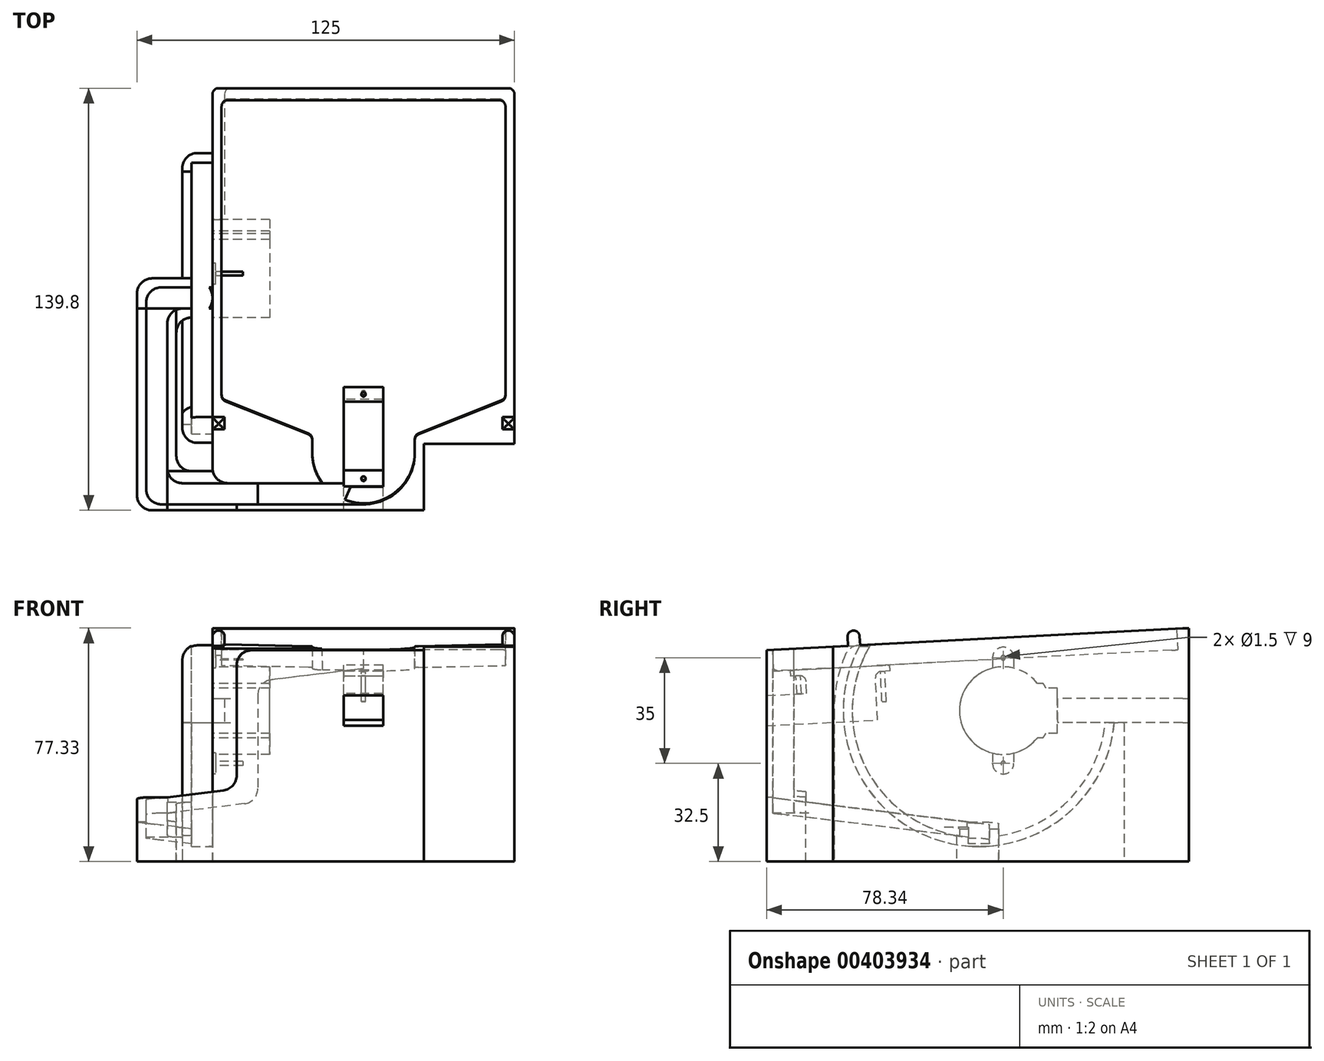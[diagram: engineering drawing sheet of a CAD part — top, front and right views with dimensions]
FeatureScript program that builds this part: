
annotation { "Feature Type Name" : "Feature", "Feature Type Description" : "" }
export const myFeature = defineFeature(function(context is Context, id is Id, definition is map)
    precondition{}
    {
        {
            var Q0;
            Q0=qCreatedBy(makeId("Right.planeOp"),FACE);
            var sketch = newSketch(context, id + "F0", { "sketchPlane" : qUnion([Q0])});
            skLineSegment(sketch, "E0", {"start": v(-65.34, 50) * mm, "end": v(-65.34, -20) * mm});
            skLineSegment(sketch, "E1", {"start": v(-65.34, -20) * mm, "end": v(74.46, -20) * mm});
            skLineSegment(sketch, "E2", {"start": v(74.46, -20) * mm, "end": v(74.46, 57.33) * mm});
            skLineSegment(sketch, "E3", {"start": v(74.46, 57.33) * mm, "end": v(-65.34, 50) * mm});
            skPoint(sketch, "E4", {"position": v(0, 53.42) * mm});
            skPoint(sketch, "E5", {"position": v(0, 46.41) * mm});
            skSolve(sketch);
        }
        {
            var Q0;
            Q0=qSketchRegion(id+"F0",true);
            extrude(context, id + "F1", {"entities" : qUnion([Q0]), "depth" : 50 * mm, "hasSecondDirection" : true, "secondDirectionOppositeDirection" : true, "secondDirectionDepth" : 50 * mm});
        }
        {
            var Q0;
            Q0=makeQuery(id+"F1.opExtrude","SWEPT_FACE",FACE,{"disambiguationData":[OSD([sQuery(id+"F0.wireOp",EDGE,"E3")])]});
            var sketch = newSketch(context, id + "F2", { "sketchPlane" : qUnion([Q0])});
            skPoint(sketch, "E6.endSnap0", {"position": v(0, -57.54) * mm});
            skPoint(sketch, "E6.end.orphan", {"position": v(0, -83) * mm});
            skPoint(sketch, "E7.orphan", {"position": v(-48, -57.54) * mm});
            skPoint(sketch, "E8.orphan", {"position": v(48, -57.54) * mm});
            skLineSegment(sketch, "E9.0", {"start": v(47, 73.36) * mm, "end": v(-47, 73.36) * mm});
            skLineSegment(sketch, "E9.1", {"start": v(47, 73.36) * mm, "end": v(47, -25.96) * mm});
            skLineSegment(sketch, "E9.2", {"start": v(-47, 73.36) * mm, "end": v(-47, -25.96) * mm});
            skLineSegment(sketch, "E9.3", {"start": v(17, -37.96) * mm, "end": v(47, -25.96) * mm});
            skLineSegment(sketch, "E9.4", {"start": v(-17, -37.96) * mm, "end": v(-47, -25.96) * mm});
            skLineSegment(sketch, "E9.5", {"start": v(-17, -43.64) * mm, "end": v(-17, -37.96) * mm});
            skArc(sketch, "E9.6", {"start": v(-17, -43.64) * mm, "mid": v(0, -60.64) * mm, "end": v(17, -43.64) * mm});
            skLineSegment(sketch, "E9.7", {"start": v(17, -43.64) * mm, "end": v(17, -37.96) * mm});
            skPoint(sketch, "E10.bottom.end.orphan", {"position": v(-48, 78.46) * mm});
            skPoint(sketch, "E10.bottom.start.orphan", {"position": v(48, 78.46) * mm});
            skPoint(sketch, "E11", {"position": v(0, 2.8) * mm});
            skSolve(sketch);
        }
        {
            var Q0;
            Q0=makeQuery(id+"F2.imprint","IMPRINT",FACE,{"disambiguationData":[TD([[makeQuery(id+"F2.imprint","IMPRINT",EDGE,{"derivedFrom":sQuery(id+"F2.wireOp",EDGE,"E9.0")}),1.0]])]});
            cPlane(context, id + "F3", {"entities" : qUnion([Q0]), "cplaneType" : CPlaneType.OFFSET, "offset" : 7 * mm, "oppositeDirection" : true, "width" : 150 * mm, "height" : 150 * mm});
        }
        {
            var Q0;
            Q0=qCreatedBy(id+"F3.planeOp",FACE);
            var sketch = newSketch(context, id + "F4", { "sketchPlane" : qUnion([Q0])});
            skPoint(sketch, "E12", {"position": v(0, 2.43) * mm});
            skPoint(sketch, "E13.endSnap0", {"position": v(0, -58.41) * mm});
            skPoint(sketch, "E13.end.orphan", {"position": v(0, -83.88) * mm});
            skPoint(sketch, "E14.orphan", {"position": v(-48, -58.41) * mm});
            skPoint(sketch, "E15.orphan", {"position": v(48, -58.41) * mm});
            skLineSegment(sketch, "E16.0", {"start": v(47, 73.36) * mm, "end": v(-47, 73.36) * mm});
            skLineSegment(sketch, "E16.1", {"start": v(47, 73.36) * mm, "end": v(47, -25.96) * mm});
            skLineSegment(sketch, "E16.2", {"start": v(-47, 73.36) * mm, "end": v(-47, -25.96) * mm});
            skLineSegment(sketch, "E16.3", {"start": v(17, -37.96) * mm, "end": v(47, -25.96) * mm});
            skLineSegment(sketch, "E16.4", {"start": v(-17, -37.96) * mm, "end": v(-47, -25.96) * mm});
            skLineSegment(sketch, "E16.5", {"start": v(-17, -43.64) * mm, "end": v(-17, -37.96) * mm});
            skArc(sketch, "E16.6", {"start": v(-17, -43.64) * mm, "mid": v(0, -60.64) * mm, "end": v(17, -43.64) * mm});
            skLineSegment(sketch, "E16.7", {"start": v(17, -43.64) * mm, "end": v(17, -37.96) * mm});
            skPoint(sketch, "E17.bottom.end.orphan", {"position": v(-48, 77.59) * mm});
            skPoint(sketch, "E17.bottom.start.orphan", {"position": v(48, 77.59) * mm});
            skSolve(sketch);
        }
        {
            var Q1;
            Q1=qSketchRegion(id+"F2",true);
            var Q2;
            Q2=qSketchRegion(id+"F4",true);
            loft(context, id + "F5", {"operationType" : NewBodyOperationType.REMOVE, "sheetProfilesArray" : [{ "sheetProfileEntities" : qUnion([Q1]) }, { "sheetProfileEntities" : qUnion([Q2]) }]});
        }
        {
            var Q0;
            Q0=makeQuery(id+"F1.opExtrude","CAP_FACE",FACE,{"disambiguationData":[OSD([sQuery(id+"F0.wireOp",EDGE,"E0"),sQuery(id+"F0.wireOp",EDGE,"E1"),sQuery(id+"F0.wireOp",EDGE,"E2"),sQuery(id+"F0.wireOp",EDGE,"E3")])],"isStart":true});
            var sketch = newSketch(context, id + "F6", { "sketchPlane" : qUnion([Q0])});
            skArc(sketch, "E18", {"start": v(-24.37, 21) * mm, "mid": v(1.5, 30) * mm, "end": v(-24.37, 39) * mm});
            skPoint(sketch, "E19", {"position": v(-5, 30) * mm});
            skLineSegment(sketch, "E20.bottom", {"start": v(-31, 22.5) * mm, "end": v(-27.13, 22.5) * mm});
            skLineSegment(sketch, "E20.top", {"start": v(-31, 37.5) * mm, "end": v(-27.13, 37.5) * mm});
            skLineSegment(sketch, "E20.left", {"start": v(-31, 22.5) * mm, "end": v(-31, 37.5) * mm});
            skArc(sketch, "E21", {"start": v(-26.23, 39) * mm, "mid": v(-26.7, 38.26) * mm, "end": v(-27.13, 37.5) * mm});
            skLineSegment(sketch, "E22.bottom", {"start": v(-26.23, 39) * mm, "end": v(-24.37, 39) * mm});
            skLineSegment(sketch, "E22.top", {"start": v(-26.23, 21) * mm, "end": v(-24.37, 21) * mm});
            skArc(sketch, "E23.trimOffspring", {"start": v(-27.13, 22.5) * mm, "mid": v(-26.7, 21.74) * mm, "end": v(-26.23, 21) * mm});
            skSolve(sketch);
        }
        {
            var Q0;
            Q0=qSketchRegion(id+"F6",true);
            extrude(context, id + "F7", {"entities" : qUnion([Q0]), "operationType" : NewBodyOperationType.REMOVE, "oppositeDirection" : true, "depth" : 19 * mm});
        }
        {
            var Q0;
            Q0=makeQuery(id+"F1.opExtrude","CAP_FACE",FACE,{"disambiguationData":[OSD([sQuery(id+"F0.wireOp",EDGE,"E0"),sQuery(id+"F0.wireOp",EDGE,"E1"),sQuery(id+"F0.wireOp",EDGE,"E2"),sQuery(id+"F0.wireOp",EDGE,"E3")])],"isStart":true});
            var sketch = newSketch(context, id + "F8", { "sketchPlane" : qUnion([Q0])});
            skLineSegment(sketch, "E24", {"start": v(-13, 47.5) * mm, "end": v(-13, 12.5) * mm});
            skPoint(sketch, "E25", {"position": v(-13, 30) * mm});
            skArc(sketch, "E26.0.startCap", {"start": v(-16.5, 47.5) * mm, "mid": v(-13, 51) * mm, "end": v(-9.5, 47.5) * mm});
            skArc(sketch, "E26.0.endCap", {"start": v(-9.5, 12.5) * mm, "mid": v(-13, 9) * mm, "end": v(-16.5, 12.5) * mm});
            skLineSegment(sketch, "E26.0.left", {"start": v(-9.5, 47.5) * mm, "end": v(-9.5, 12.5) * mm});
            skLineSegment(sketch, "E26.0.right", {"start": v(-16.5, 47.5) * mm, "end": v(-16.5, 12.5) * mm});
            skSolve(sketch);
        }
        {
            var Q0;
            Q0=qSketchRegion(id+"F8",true);
            extrude(context, id + "F9", {"entities" : qUnion([Q0]), "operationType" : NewBodyOperationType.REMOVE, "oppositeDirection" : true, "depth" : 1 * mm});
        }
        {
            var Q0;
            Q0=makeQuery(id+"F1.opExtrude","CAP_FACE",FACE,{"disambiguationData":[OSD([sQuery(id+"F0.wireOp",EDGE,"E0"),sQuery(id+"F0.wireOp",EDGE,"E1"),sQuery(id+"F0.wireOp",EDGE,"E2"),sQuery(id+"F0.wireOp",EDGE,"E3")])],"isStart":true});
            var sketch = newSketch(context, id + "F10", { "sketchPlane" : qUnion([Q0])});
            skLineSegment(sketch, "E27.bottom", {"start": v(-81, 34) * mm, "end": v(-21, 34) * mm});
            skLineSegment(sketch, "E27.top", {"start": v(-81, 26) * mm, "end": v(-21, 26) * mm});
            skLineSegment(sketch, "E27.left", {"start": v(-81, 34) * mm, "end": v(-81, 26) * mm});
            skLineSegment(sketch, "E27.right", {"start": v(-21, 34) * mm, "end": v(-21, 26) * mm});
            skPoint(sketch, "E27.middle", {"position": v(-51, 30) * mm});
            skSolve(sketch);
        }
        {
            var Q0;
            Q0=qSketchRegion(id+"F10",true);
            extrude(context, id + "F11", {"entities" : qUnion([Q0]), "operationType" : NewBodyOperationType.REMOVE, "oppositeDirection" : true, "depth" : 4 * mm});
        }
        {
            var Q0;
            Q0=qCreatedBy(makeId("Front.planeOp"),FACE);
            cPlane(context, id + "F12", {"entities" : qUnion([Q0]), "cplaneType" : CPlaneType.OFFSET, "offset" : 5 * mm, "oppositeDirection" : true, "width" : 150 * mm, "height" : 150 * mm});
        }
        {
            var Q0;
            Q0=qCreatedBy(id+"F12.planeOp",FACE);
            var sketch = newSketch(context, id + "F13", { "sketchPlane" : qUnion([Q0])});
            skLineSegment(sketch, "E28", {"start": v(-50, -20) * mm, "end": v(-75, -20) * mm});
            skLineSegment(sketch, "E29", {"start": v(-50, -9.96) * mm, "end": v(-75, -6.9) * mm});
            skLineSegment(sketch, "E30", {"start": v(-75, -20) * mm, "end": v(-75, -6.9) * mm});
            skLineSegment(sketch, "E31", {"start": v(-50, -20) * mm, "end": v(-50, -9.96) * mm});
            skSolve(sketch);
        }
        {
            var Q0;
            Q0=qSketchRegion(id+"F13",true);
            extrude(context, id + "F14", {"entities" : qUnion([Q0]), "operationType" : NewBodyOperationType.ADD, "depth" : 6.5 * mm, "hasSecondDirection" : true, "secondDirectionOppositeDirection" : true, "secondDirectionDepth" : 6.5 * mm});
        }
        {
            var Q0;
            Q0=makeQuery(id+"F2.imprint","IMPRINT",FACE,{"disambiguationData":[TD([[makeQuery(id+"F2.imprint","IMPRINT",EDGE,{"derivedFrom":sQuery(id+"F2.wireOp",EDGE,"E9.0")}),1.0]])]});
            var sketch = newSketch(context, id + "F15", { "sketchPlane" : qUnion([Q0])});
            skLineSegment(sketch, "E32.bottom", {"start": v(6.5, -50.14) * mm, "end": v(-6.5, -50.14) * mm});
            skLineSegment(sketch, "E32.top", {"start": v(6.5, -27.14) * mm, "end": v(-6.5, -27.14) * mm});
            skLineSegment(sketch, "E32.left", {"start": v(6.5, -50.14) * mm, "end": v(6.5, -27.14) * mm});
            skLineSegment(sketch, "E32.right", {"start": v(-6.5, -50.14) * mm, "end": v(-6.5, -27.14) * mm});
            skPoint(sketch, "E32.middle", {"position": v(0, -38.64) * mm});
            skSolve(sketch);
        }
        {
            var Q0;
            Q0=qSketchRegion(id+"F15",true);
            extrude(context, id + "F16", {"entities" : qUnion([Q0]), "operationType" : NewBodyOperationType.REMOVE, "oppositeDirection" : true, "depth" : 25 * mm});
        }
        {
            var Q0;
            Q0=makeQuery(id+"F2.imprint","IMPRINT",FACE,{"disambiguationData":[TD([[makeQuery(id+"F2.imprint","IMPRINT",EDGE,{"derivedFrom":sQuery(id+"F2.wireOp",EDGE,"E9.0")}),1.0]])]});
            var sketch = newSketch(context, id + "F17", { "sketchPlane" : qUnion([Q0])});
            skLineSegment(sketch, "E33.bottom", {"start": v(6.5, -22.14) * mm, "end": v(-6.5, -22.14) * mm});
            skLineSegment(sketch, "E33.top", {"start": v(6.5, -55.14) * mm, "end": v(-6.5, -55.14) * mm});
            skLineSegment(sketch, "E33.left", {"start": v(6.5, -22.14) * mm, "end": v(6.5, -55.14) * mm});
            skLineSegment(sketch, "E33.right", {"start": v(-6.5, -22.14) * mm, "end": v(-6.5, -55.14) * mm});
            skPoint(sketch, "E33.middle", {"position": v(0, -38.64) * mm});
            skSolve(sketch);
        }
        {
            var Q0;
            Q0=qSketchRegion(id+"F17",true);
            extrude(context, id + "F18", {"entities" : qUnion([Q0]), "operationType" : NewBodyOperationType.REMOVE, "oppositeDirection" : true, "depth" : 9 * mm});
        }
        {
            var Q0;
            Q0=makeQuery(id+"FUqeBeKpT4LYNuk_1.boolean.opBoolean","MERGE",FACE,{"derivedFrom":[makeQuery(id+"F1.opExtrude","SWEPT_FACE",FACE,{"disambiguationData":[OSD([sQuery(id+"F0.wireOp",EDGE,"E0")])]}),makeQuery(id+"F61UTTqEWsXgY2D_1.opExtrude","SWEPT_FACE",FACE,{"disambiguationData":[OSD([sQuery(id+"F9Du9WT9e9JY5Dl_1.wireOp",EDGE,"sJgd1tPc-9qsz-vVnT-TqeQ-4TYIqpoZbmCu")])]}),makeQuery(id+"FUqeBeKpT4LYNuk_1.opExtrude","CAP_FACE",FACE,{"disambiguationData":[OSD([sQuery(id+"Fu5qXJoa0auTo1w_1.wireOp",EDGE,"depduNjt-3aMR-BOii-vv3o-0Txvqa5xbjUM"),sQuery(id+"Fu5qXJoa0auTo1w_1.wireOp",EDGE,"YClS0oY7-eXia-WmQ4-NOUT-qmrgQAcRW2ul"),sQuery(id+"Fu5qXJoa0auTo1w_1.wireOp",EDGE,"FjPESpCu-MEkZ-X1k0-rLkk-jPPFp3MV8du9"),sQuery(id+"Fu5qXJoa0auTo1w_1.wireOp",EDGE,"T3NzeVoH-fv4R-7HJz-S144-zwuEIWOQCuFN")])],"isStart":true})]});
            var sketch = newSketch(context, id + "F19", { "sketchPlane" : qUnion([Q0])});
            skLineSegment(sketch, "E34.bottom", {"start": v(50, -20) * mm, "end": v(20, -20) * mm});
            skLineSegment(sketch, "E34.top", {"start": v(50, 60) * mm, "end": v(20, 60) * mm});
            skLineSegment(sketch, "E34.left", {"start": v(50, -20) * mm, "end": v(50, 60) * mm});
            skLineSegment(sketch, "E34.right", {"start": v(20, -20) * mm, "end": v(20, 60) * mm});
            skSolve(sketch);
        }
        {
            var Q0;
            Q0=qSketchRegion(id+"F19",true);
            extrude(context, id + "F20", {"entities" : qUnion([Q0]), "operationType" : NewBodyOperationType.REMOVE, "oppositeDirection" : true, "depth" : 22 * mm});
        }
        {
            var Q0;
            Q0=makeQuery(id+"F16.boolean.opBoolean","COPY",FACE,{"derivedFrom":makeQuery(id+"F16.opExtrude","SWEPT_FACE",FACE,{"disambiguationData":[OSD([sQuery(id+"F15.wireOp",EDGE,"E32.bottom")])]})});
            var sketch = newSketch(context, id + "F21", { "sketchPlane" : qUnion([Q0])});
            skLineSegment(sketch, "E35.bottom", {"start": v(-6.5, 28.35) * mm, "end": v(6.5, 28.35) * mm});
            skLineSegment(sketch, "E35.top", {"start": v(-6.5, 38.35) * mm, "end": v(6.5, 38.35) * mm});
            skLineSegment(sketch, "E35.left", {"start": v(-6.5, 28.35) * mm, "end": v(-6.5, 38.35) * mm});
            skLineSegment(sketch, "E35.right", {"start": v(6.5, 28.35) * mm, "end": v(6.5, 38.35) * mm});
            skSolve(sketch);
        }
        {
            var Q0;
            Q0=qSketchRegion(id+"F21",true);
            extrude(context, id + "F22", {"entities" : qUnion([Q0]), "operationType" : NewBodyOperationType.REMOVE, "oppositeDirection" : true, "depth" : 25 * mm});
        }
        {
            var Q0;
            Q0=qCreatedBy(id+"F12.planeOp",FACE);
            var sketch = newSketch(context, id + "F23", { "sketchPlane" : qUnion([Q0])});
            skLineSegment(sketch, "E36", {"start": v(-50, -6.3) * mm, "end": v(-50, -15) * mm});
            skLineSegment(sketch, "E37", {"start": v(-50, -15) * mm, "end": v(-72, -12.3) * mm});
            skLineSegment(sketch, "E38", {"start": v(-72, -12.3) * mm, "end": v(-72, -6.3) * mm});
            skLineSegment(sketch, "E39", {"start": v(-72, -6.3) * mm, "end": v(-50, -6.3) * mm});
            skSolve(sketch);
        }
        {
            var Q0;
            Q0=qSketchRegion(id+"F23",true);
            extrude(context, id + "F24", {"entities" : qUnion([Q0]), "operationType" : NewBodyOperationType.REMOVE, "oppositeDirection" : true, "depth" : 3.5 * mm, "hasSecondDirection" : true, "secondDirectionOppositeDirection" : false, "secondDirectionDepth" : 3.5 * mm});
        }
        {
            var Q0;
            Q0=makeQuery(id+"F14.opExtrude","SWEPT_FACE",FACE,{"disambiguationData":[OSD([sQuery(id+"F13.wireOp",EDGE,"E30")])]});
            var sketch = newSketch(context, id + "F25", { "sketchPlane" : qUnion([Q0])});
            skLineSegment(sketch, "E40", {"start": v(1.5, -20) * mm, "end": v(65.34, -20) * mm});
            skLineSegment(sketch, "E41", {"start": v(65.34, -20) * mm, "end": v(65.34, 1.31) * mm});
            skLineSegment(sketch, "E42", {"start": v(65.34, 1.31) * mm, "end": v(-1.5, -6.9) * mm});
            skLineSegment(sketch, "E43", {"start": v(-1.5, -6.9) * mm, "end": v(-1.5, -20) * mm});
            skLineSegment(sketch, "E44", {"start": v(-1.5, -20) * mm, "end": v(1.5, -20) * mm});
            skSolve(sketch);
        }
        {
            var Q0;
            Q0=qSketchRegion(id+"F25",true);
            extrude(context, id + "F26", {"entities" : qUnion([Q0]), "operationType" : NewBodyOperationType.ADD, "oppositeDirection" : true, "depth" : 13 * mm});
        }
        {
            var Q0;
            Q0=makeQuery(id+"F26.boolean.opBoolean","MERGE",FACE,{"derivedFrom":[makeQuery(id+"F14.opExtrude","SWEPT_FACE",FACE,{"disambiguationData":[OSD([sQuery(id+"F13.wireOp",EDGE,"E30")])]}),makeQuery(id+"F26.opExtrude","CAP_FACE",FACE,{"disambiguationData":[OSD([sQuery(id+"F25.wireOp",EDGE,"E40"),sQuery(id+"F25.wireOp",EDGE,"E41"),sQuery(id+"F25.wireOp",EDGE,"E42"),sQuery(id+"F25.wireOp",EDGE,"E43"),sQuery(id+"F25.wireOp",EDGE,"E44")])],"isStart":true})]});
            cPlane(context, id + "F27", {"entities" : qUnion([Q0]), "cplaneType" : CPlaneType.OFFSET, "offset" : 3 * mm, "oppositeDirection" : true, "width" : 150 * mm, "height" : 150 * mm});
        }
        {
            var Q0;
            Q0=qCreatedBy(id+"F27.planeOp",FACE);
            var sketch = newSketch(context, id + "F28", { "sketchPlane" : qUnion([Q0])});
            skLineSegment(sketch, "E45", {"start": v(-1.5, -2.4) * mm, "end": v(-1.5, -11.93) * mm});
            skLineSegment(sketch, "E46", {"start": v(-1.5, -11.93) * mm, "end": v(63.34, -3.97) * mm});
            skLineSegment(sketch, "E47", {"start": v(63.34, -3.97) * mm, "end": v(63.34, 3.33) * mm});
            skLineSegment(sketch, "E48", {"start": v(63.34, 3.33) * mm, "end": v(-1.5, 3.33) * mm});
            skLineSegment(sketch, "E49", {"start": v(-1.5, 3.33) * mm, "end": v(-1.5, -2.4) * mm});
            skSolve(sketch);
        }
        {
            var Q0;
            Q0=qSketchRegion(id+"F28",true);
            extrude(context, id + "F29", {"entities" : qUnion([Q0]), "operationType" : NewBodyOperationType.REMOVE, "oppositeDirection" : true, "depth" : 7 * mm});
        }
        {
            var Q0;
            Q0=makeQuery(id+"F1.opExtrude","SWEPT_FACE",FACE,{"disambiguationData":[OSD([sQuery(id+"F0.wireOp",EDGE,"E0")])]});
            var sketch = newSketch(context, id + "F30", { "sketchPlane" : qUnion([Q0])});
            skLineSegment(sketch, "E50", {"start": v(-50, -20) * mm, "end": v(-50, 3.16) * mm});
            skLineSegment(sketch, "E51", {"start": v(-50, 3.16) * mm, "end": v(-65, 1.31) * mm});
            skLineSegment(sketch, "E52", {"start": v(-65, 1.31) * mm, "end": v(-65, -20) * mm});
            skLineSegment(sketch, "E53", {"start": v(-65, -20) * mm, "end": v(-50, -20) * mm});
            skSolve(sketch);
        }
        {
            var Q0;
            Q0=qSketchRegion(id+"F30",true);
            extrude(context, id + "F31", {"entities" : qUnion([Q0]), "operationType" : NewBodyOperationType.ADD, "oppositeDirection" : true, "depth" : 13 * mm});
        }
        {
            var Q0;
            Q0=makeQuery(id+"F29.boolean.opBoolean","COPY",FACE,{"derivedFrom":makeQuery(id+"F29.opExtrude","SWEPT_FACE",FACE,{"disambiguationData":[OSD([sQuery(id+"F28.wireOp",EDGE,"E47")])]})});
            var sketch = newSketch(context, id + "F32", { "sketchPlane" : qUnion([Q0])});
            skLineSegment(sketch, "E54", {"start": v(65, -3.97) * mm, "end": v(65, 76.03) * mm});
            skLineSegment(sketch, "E55", {"start": v(65, 76.03) * mm, "end": v(0, 76.03) * mm});
            skLineSegment(sketch, "E56", {"start": v(0, 76.03) * mm, "end": v(0, 43.93) * mm});
            skLineSegment(sketch, "E57", {"start": v(0, 43.93) * mm, "end": v(35, 39.63) * mm});
            skLineSegment(sketch, "E58", {"start": v(35, 39.63) * mm, "end": v(35, -0.29) * mm});
            skLineSegment(sketch, "E59", {"start": v(35, -0.29) * mm, "end": v(65, -3.97) * mm});
            skSolve(sketch);
        }
        {
            var Q0;
            Q0=qSketchRegion(id+"F32",true);
            extrude(context, id + "F33", {"entities" : qUnion([Q0]), "operationType" : NewBodyOperationType.REMOVE, "depth" : 7 * mm});
        }
        {
            var Q0;
            Q0=makeQuery(id+"F33.boolean.opBoolean","MERGE",FACE,{"derivedFrom":[makeQuery(id+"F29.boolean.opBoolean","COPY",FACE,{"derivedFrom":makeQuery(id+"F29.opExtrude","SWEPT_FACE",FACE,{"disambiguationData":[OSD([sQuery(id+"F28.wireOp",EDGE,"E47")])]})}),makeQuery(id+"F33.opExtrude","CAP_FACE",FACE,{"disambiguationData":[OSD([sQuery(id+"F32.wireOp",EDGE,"E54"),sQuery(id+"F32.wireOp",EDGE,"E55"),sQuery(id+"F32.wireOp",EDGE,"E56"),sQuery(id+"F32.wireOp",EDGE,"E57"),sQuery(id+"F32.wireOp",EDGE,"E58"),sQuery(id+"F32.wireOp",EDGE,"E59")])],"isStart":true})]});
            var sketch = newSketch(context, id + "F34", { "sketchPlane" : qUnion([Q0])});
            skLineSegment(sketch, "E60", {"start": v(50, 3.16) * mm, "end": v(42, 4.14) * mm});
            skLineSegment(sketch, "E61", {"start": v(42, 4.14) * mm, "end": v(42, 50.1) * mm});
            skLineSegment(sketch, "E62", {"start": v(42, 50.1) * mm, "end": v(50, 50.1) * mm});
            skLineSegment(sketch, "E63", {"start": v(50, 50.1) * mm, "end": v(50, 3.16) * mm});
            skSolve(sketch);
        }
        {
            var Q0;
            Q0=qSketchRegion(id+"F34",true);
            extrude(context, id + "F35", {"entities" : qUnion([Q0]), "operationType" : NewBodyOperationType.REMOVE, "oppositeDirection" : true, "depth" : 3 * mm});
        }
        {
            var Q0;
            Q0=makeQuery(id+"F6.imprint","IMPRINT",FACE,{"disambiguationData":[TD([[makeQuery(id+"F6.imprint","IMPRINT",EDGE,{"derivedFrom":sQuery(id+"F6.wireOp",EDGE,"E18")}),-1.0]])]});
            var sketch = newSketch(context, id + "F36", { "sketchPlane" : qUnion([Q0])});
            skArc(sketch, "E64", {"start": v(-49.82, 26) * mm, "mid": v(-37.7, -0.92) * mm, "end": v(-11.5, -14.53) * mm});
            skArc(sketch, "E65", {"start": v(43, 30) * mm, "mid": v(41.72, 41.01) * mm, "end": v(37.95, 51.44) * mm});
            skLineSegment(sketch, "E66", {"start": v(37.95, 51.44) * mm, "end": v(34.47, 51.62) * mm});
            skPoint(sketch, "E67", {"position": v(43, 30) * mm});
            skLineSegment(sketch, "E68", {"start": v(43, 30) * mm, "end": v(43, -20) * mm});
            skLineSegment(sketch, "E69", {"start": v(-53, 26) * mm, "end": v(-53, -20) * mm});
            skLineSegment(sketch, "E70", {"start": v(-53, -20) * mm, "end": v(43, -20) * mm});
            skLineSegment(sketch, "E71", {"start": v(-53, 26) * mm, "end": v(-49.82, 26) * mm});
            skLineSegment(sketch, "E72", {"start": v(-11.5, -14.53) * mm, "end": v(-11.5, -20) * mm});
            skLineSegment(sketch, "E73", {"start": v(1.5, -14.53) * mm, "end": v(1.5, -20) * mm});
            skArc(sketch, "E74.trimOffspring", {"start": v(1.5, -14.53) * mm, "mid": v(35.28, 9.93) * mm, "end": v(34.47, 51.62) * mm});
            skSolve(sketch);
        }
        {
            var Q0;
            Q0=qSketchRegion(id+"F36",true);
            extrude(context, id + "F37", {"entities" : qUnion([Q0]), "operationType" : NewBodyOperationType.ADD, "depth" : 10 * mm});
        }
        {
            var Q0;
            Q0=makeQuery(id+"F37.opExtrude","CAP_FACE",FACE,{"disambiguationData":[OSD([sQuery(id+"F36.wireOp",EDGE,"E64"),sQuery(id+"F36.wireOp",EDGE,"E69"),sQuery(id+"F36.wireOp",EDGE,"E70"),sQuery(id+"F36.wireOp",EDGE,"E71"),sQuery(id+"F36.wireOp",EDGE,"E72")])],"isStart":false});
            var sketch = newSketch(context, id + "F38", { "sketchPlane" : qUnion([Q0])});
            skArc(sketch, "E75", {"start": v(1.5, -14.53) * mm, "mid": v(35.28, 9.93) * mm, "end": v(34.47, 51.62) * mm});
            skArc(sketch, "E76", {"start": v(1.5, -11.5) * mm, "mid": v(33.1, 12.3) * mm, "end": v(30.9, 51.8) * mm});
            skLineSegment(sketch, "E77", {"start": v(-49.82, 26) * mm, "end": v(-46.8, 26) * mm});
            skLineSegment(sketch, "E78", {"start": v(34.47, 51.62) * mm, "end": v(30.9, 51.8) * mm});
            skLineSegment(sketch, "E79", {"start": v(-11.5, -14.53) * mm, "end": v(-11.5, -11.5) * mm});
            skLineSegment(sketch, "E80", {"start": v(1.5, -14.53) * mm, "end": v(1.5, -11.5) * mm});
            skArc(sketch, "E81.trimOffspring", {"start": v(-46.8, 26) * mm, "mid": v(-35.58, 1.2) * mm, "end": v(-11.5, -11.5) * mm});
            skArc(sketch, "E82.trimOffspring", {"start": v(-49.82, 26) * mm, "mid": v(-37.7, -0.92) * mm, "end": v(-11.5, -14.53) * mm});
            skSolve(sketch);
        }
        {
            var Q0;
            Q0=qSketchRegion(id+"F38",true);
            extrude(context, id + "F39", {"entities" : qUnion([Q0]), "operationType" : NewBodyOperationType.ADD, "oppositeDirection" : true, "depth" : 3 * mm});
        }
        {
            var Q0;
            Q0=makeQuery(id+"F6.imprint","IMPRINT",FACE,{"disambiguationData":[TD([[makeQuery(id+"F6.imprint","IMPRINT",EDGE,{"derivedFrom":sQuery(id+"F6.wireOp",EDGE,"E18")}),-1.0]])]});
            var sketch = newSketch(context, id + "F40", { "sketchPlane" : qUnion([Q0])});
            skCircle(sketch, "E83", {"center": v(-5, 30) * mm, "radius": 45 * mm});
            skSolve(sketch);
        }
        {
            var Q0;
            Q0=qSketchRegion(id+"F40",true);
            extrude(context, id + "F41", {"entities" : qUnion([Q0]), "operationType" : NewBodyOperationType.REMOVE, "depth" : 7 * mm});
        }
        {
            var Q0;
            Q0=makeQuery(id+"F20.boolean.opBoolean","COPY",EDGE,{"derivedFrom":makeQuery(id+"F20.opExtrude","CAP_EDGE",EDGE,{"disambiguationData":[OSD([sQuery(id+"F19.wireOp",EDGE,"E34.right")])],"isStart":true})});
            var Q1;
            Q1=makeQuery(id+"F20.boolean.opBoolean","COPY",EDGE,{"derivedFrom":makeQuery(id+"F20.opExtrude","CAP_EDGE",EDGE,{"disambiguationData":[OSD([sQuery(id+"F19.wireOp",EDGE,"E34.left")])],"isStart":false})});
            var Q2;
            Q2=makeQuery(id+"F37.opExtrude","CAP_EDGE",EDGE,{"disambiguationData":[OSD([sQuery(id+"F36.wireOp",EDGE,"E69")])],"isStart":false});
            var Q3;
            Q3=makeQuery(id+"F37.opExtrude","CAP_EDGE",EDGE,{"disambiguationData":[OSD([sQuery(id+"F36.wireOp",EDGE,"E68")])],"isStart":false});
            var Q4;
            Q4=makeQuery(id+"F37.opExtrude","SWEPT_EDGE",EDGE,{"disambiguationData":[OSD([sQuery(id+"F0.wireOp",EDGE,"E3"),sQuery(id+"F36.wireOp",EDGE,"E65"),sQuery(id+"F36.wireOp",EDGE,"E66")])]});
            var Q5;
            Q5=makeQuery(id+"F39.boolean.opBoolean","MERGE",EDGE,{"derivedFrom":[makeQuery(id+"F37.opExtrude","CAP_EDGE",EDGE,{"disambiguationData":[OSD([sQuery(id+"F36.wireOp",EDGE,"E66")])],"isStart":false}),makeQuery(id+"F39.opExtrude","CAP_EDGE",EDGE,{"disambiguationData":[OSD([sQuery(id+"F38.wireOp",EDGE,"E78")])],"isStart":true})]});
            var Q6;
            Q6=makeQuery(id+"F14.opExtrude","CAP_EDGE",EDGE,{"disambiguationData":[OSD([sQuery(id+"F13.wireOp",EDGE,"E30")])],"isStart":true});
            var Q7;
            Q7=makeQuery(id+"F26.opExtrude","CAP_EDGE",EDGE,{"disambiguationData":[OSD([sQuery(id+"F25.wireOp",EDGE,"E41")])],"isStart":true});
            var Q8;
            Q8=makeQuery(id+"F35.boolean.opBoolean","INTERSECT",EDGE,{"derivedFrom":[makeQuery(id+"F1.opExtrude","SWEPT_FACE",FACE,{"disambiguationData":[OSD([sQuery(id+"F0.wireOp",EDGE,"E3")])]}),makeQuery(id+"F35.opExtrude","SWEPT_FACE",FACE,{"disambiguationData":[OSD([sQuery(id+"F34.wireOp",EDGE,"E61")])]})]});
            var Q9;
            Q9=makeQuery(id+"F33.boolean.opBoolean","COPY",EDGE,{"derivedFrom":makeQuery(id+"F33.opExtrude","CAP_EDGE",EDGE,{"disambiguationData":[OSD([sQuery(id+"F32.wireOp",EDGE,"E54")])],"isStart":false})});
            var Q10;
            Q10=makeQuery(id+"F31.boolean.opBoolean","INTERSECT",EDGE,{"derivedFrom":[makeQuery(id+"F26.opExtrude","CAP_FACE",FACE,{"disambiguationData":[OSD([sQuery(id+"F25.wireOp",EDGE,"E40"),sQuery(id+"F25.wireOp",EDGE,"E41"),sQuery(id+"F25.wireOp",EDGE,"E42"),sQuery(id+"F25.wireOp",EDGE,"E43"),sQuery(id+"F25.wireOp",EDGE,"E44")])],"isStart":false}),makeQuery(id+"F31.opExtrude","CAP_FACE",FACE,{"disambiguationData":[OSD([sQuery(id+"F30.wireOp",EDGE,"E50"),sQuery(id+"F30.wireOp",EDGE,"E51"),sQuery(id+"F30.wireOp",EDGE,"E52"),sQuery(id+"F30.wireOp",EDGE,"E53")])],"isStart":false})]});
            var Q11;
            Q11=makeQuery(id+"F29.boolean.opBoolean","COPY",EDGE,{"derivedFrom":makeQuery(id+"F29.opExtrude","CAP_EDGE",EDGE,{"disambiguationData":[OSD([sQuery(id+"F28.wireOp",EDGE,"E47")])],"isStart":true})});
            var Q12;
            Q12=makeQuery(id+"F26.boolean.opBoolean","INTERSECT",EDGE,{"derivedFrom":[makeQuery(id+"F14.opExtrude","CAP_FACE",FACE,{"disambiguationData":[OSD([sQuery(id+"F13.wireOp",EDGE,"E28"),sQuery(id+"F13.wireOp",EDGE,"E29"),sQuery(id+"F13.wireOp",EDGE,"E30"),sQuery(id+"F13.wireOp",EDGE,"E31")])],"isStart":false}),makeQuery(id+"F26.opExtrude","CAP_FACE",FACE,{"disambiguationData":[OSD([sQuery(id+"F25.wireOp",EDGE,"E40"),sQuery(id+"F25.wireOp",EDGE,"E41"),sQuery(id+"F25.wireOp",EDGE,"E42"),sQuery(id+"F25.wireOp",EDGE,"E43"),sQuery(id+"F25.wireOp",EDGE,"E44")])],"isStart":false})]});
            var Q13;
            Q13=makeQuery(id+"F24.boolean.opBoolean","COPY",EDGE,{"derivedFrom":makeQuery(id+"F24.opExtrude","CAP_EDGE",EDGE,{"disambiguationData":[OSD([sQuery(id+"F23.wireOp",EDGE,"E38")])],"isStart":false})});
            var Q14;
            Q14=makeQuery(id+"F29.boolean.opBoolean","COPY",EDGE,{"derivedFrom":makeQuery(id+"F29.opExtrude","CAP_EDGE",EDGE,{"disambiguationData":[OSD([sQuery(id+"F28.wireOp",EDGE,"E45"),sQuery(id+"F28.wireOp",EDGE,"E49")])],"isStart":false})});
            var Q15;
            Q15=makeQuery(id+"F35.boolean.opBoolean","COPY",EDGE,{"derivedFrom":makeQuery(id+"F35.opExtrude","SWEPT_EDGE",EDGE,{"disambiguationData":[OSD([sQuery(id+"F34.wireOp",EDGE,"E60"),sQuery(id+"F34.wireOp",EDGE,"E61")])]})});
            var Q16;
            Q16=makeQuery(id+"F33.boolean.opBoolean","COPY",EDGE,{"derivedFrom":makeQuery(id+"F33.opExtrude","SWEPT_EDGE",EDGE,{"disambiguationData":[OSD([sQuery(id+"F32.wireOp",EDGE,"E58"),sQuery(id+"F32.wireOp",EDGE,"E59")])]})});
            var Q17;
            Q17=makeQuery(id+"F33.boolean.opBoolean","INTERSECT",EDGE,{"derivedFrom":[makeQuery(id+"F24.boolean.opBoolean","MERGE",FACE,{"derivedFrom":[makeQuery(id+"F1.opExtrude","CAP_FACE",FACE,{"disambiguationData":[OSD([sQuery(id+"F0.wireOp",EDGE,"E0"),sQuery(id+"F0.wireOp",EDGE,"E1"),sQuery(id+"F0.wireOp",EDGE,"E2"),sQuery(id+"F0.wireOp",EDGE,"E3")])],"isStart":true}),makeQuery(id+"F24.opExtrude","SWEPT_FACE",FACE,{"disambiguationData":[OSD([sQuery(id+"F23.wireOp",EDGE,"E36")])]})]}),makeQuery(id+"F33.opExtrude","CAP_FACE",FACE,{"disambiguationData":[OSD([sQuery(id+"F32.wireOp",EDGE,"E54"),sQuery(id+"F32.wireOp",EDGE,"E55"),sQuery(id+"F32.wireOp",EDGE,"E56"),sQuery(id+"F32.wireOp",EDGE,"E57"),sQuery(id+"F32.wireOp",EDGE,"E58"),sQuery(id+"F32.wireOp",EDGE,"E59")])],"isStart":false})]});
            var Q18;
            Q18=makeQuery(id+"F33.boolean.opBoolean","COPY",EDGE,{"derivedFrom":makeQuery(id+"F33.opExtrude","SWEPT_EDGE",EDGE,{"disambiguationData":[OSD([sQuery(id+"F32.wireOp",EDGE,"E57"),sQuery(id+"F32.wireOp",EDGE,"E58")])]})});
            fillet(context, id + "F42", {"entities" : qUnion([Q0, Q1, Q2, Q3, Q4, Q5, Q6, Q7, Q8, Q9, Q10, Q11, Q12, Q13, Q14, Q15, Q16, Q17, Q18]), "radius" : 5 * mm, "tangentPropagation" : true, "allowEdgeOverflow" : false});
        }
        {
            var Q0;
            Q0=makeQuery(id+"F5.boolean.opBoolean","COPY",EDGE,{"derivedFrom":makeQuery(id+"F5.opLoft","SWEPT_EDGE",EDGE,{"disambiguationData":[OSD([sQuery(id+"F2.wireOp",EDGE,"E9.0"),sQuery(id+"F2.wireOp",EDGE,"E9.2"),sQuery(id+"F4.wireOp",EDGE,"E16.0"),sQuery(id+"F4.wireOp",EDGE,"E16.2")])]})});
            var Q1;
            Q1=makeQuery(id+"F5.boolean.opBoolean","COPY",EDGE,{"derivedFrom":makeQuery(id+"F5.opLoft","SWEPT_EDGE",EDGE,{"disambiguationData":[OSD([sQuery(id+"F2.wireOp",EDGE,"E9.0"),sQuery(id+"F2.wireOp",EDGE,"E9.1"),sQuery(id+"F4.wireOp",EDGE,"E16.0"),sQuery(id+"F4.wireOp",EDGE,"E16.1")])]})});
            var Q2;
            Q2=makeQuery(id+"F5.boolean.opBoolean","COPY",EDGE,{"derivedFrom":makeQuery(id+"F5.opLoft","SWEPT_EDGE",EDGE,{"disambiguationData":[OSD([sQuery(id+"F2.wireOp",EDGE,"E9.2"),sQuery(id+"F2.wireOp",EDGE,"E9.4"),sQuery(id+"F4.wireOp",EDGE,"E16.2"),sQuery(id+"F4.wireOp",EDGE,"E16.4")])]})});
            var Q3;
            Q3=makeQuery(id+"F5.boolean.opBoolean","COPY",EDGE,{"derivedFrom":makeQuery(id+"F5.opLoft","SWEPT_EDGE",EDGE,{"disambiguationData":[OSD([sQuery(id+"F2.wireOp",EDGE,"E9.1"),sQuery(id+"F2.wireOp",EDGE,"E9.3"),sQuery(id+"F4.wireOp",EDGE,"E16.1"),sQuery(id+"F4.wireOp",EDGE,"E16.3")])]})});
            var Q4;
            Q4=makeQuery(id+"F5.boolean.opBoolean","COPY",EDGE,{"derivedFrom":makeQuery(id+"F5.opLoft","SWEPT_EDGE",EDGE,{"disambiguationData":[OSD([sQuery(id+"F2.wireOp",EDGE,"E9.3"),sQuery(id+"F2.wireOp",EDGE,"E9.7"),sQuery(id+"F4.wireOp",EDGE,"E16.3"),sQuery(id+"F4.wireOp",EDGE,"E16.7")])]})});
            var Q5;
            Q5=makeQuery(id+"F5.boolean.opBoolean","COPY",EDGE,{"derivedFrom":makeQuery(id+"F5.opLoft","SWEPT_EDGE",EDGE,{"disambiguationData":[OSD([sQuery(id+"F2.wireOp",EDGE,"E9.4"),sQuery(id+"F2.wireOp",EDGE,"E9.5"),sQuery(id+"F4.wireOp",EDGE,"E16.4"),sQuery(id+"F4.wireOp",EDGE,"E16.5")])]})});
            var Q6;
            {var subQ0=sQuery(id+"F6.wireOp",EDGE,"E18");Q6=makeQuery(id+"F9.boolean.opBoolean","SPLIT",EDGE,{"disambiguationData":[TD([makeQuery(id+"F7.boolean.opBoolean","COPY",FACE,{"derivedFrom":makeQuery(id+"F7.opExtrude","SWEPT_FACE",FACE,{"disambiguationData":[OSD([sQuery(id+"F6.wireOp",EDGE,"E22.bottom")])]})})])],"derivedFrom":makeQuery(id+"F7.boolean.opBoolean","COPY",EDGE,{"derivedFrom":makeQuery(id+"F7.opExtrude","CAP_EDGE",EDGE,{"disambiguationData":[OSD([subQ0])],"isStart":true})})});}
            var Q7;
            Q7=makeQuery(id+"F7.boolean.opBoolean","COPY",EDGE,{"derivedFrom":makeQuery(id+"F7.opExtrude","CAP_EDGE",EDGE,{"disambiguationData":[OSD([sQuery(id+"F6.wireOp",EDGE,"E20.bottom")])],"isStart":true})});
            var Q8;
            Q8=makeQuery(id+"F7.boolean.opBoolean","COPY",EDGE,{"derivedFrom":makeQuery(id+"F7.opExtrude","CAP_EDGE",EDGE,{"disambiguationData":[OSD([sQuery(id+"F6.wireOp",EDGE,"E20.top")])],"isStart":true})});
            var Q9;
            {var subQ0=sQuery(id+"F6.wireOp",EDGE,"E20.left");Q9=makeQuery(id+"F11.boolean.opBoolean","SPLIT",EDGE,{"disambiguationData":[TD([makeQuery(id+"F7.boolean.opBoolean","COPY",FACE,{"derivedFrom":makeQuery(id+"F7.opExtrude","SWEPT_FACE",FACE,{"disambiguationData":[OSD([sQuery(id+"F6.wireOp",EDGE,"E20.top")])]})})])],"derivedFrom":makeQuery(id+"F7.boolean.opBoolean","COPY",EDGE,{"derivedFrom":makeQuery(id+"F7.opExtrude","CAP_EDGE",EDGE,{"disambiguationData":[OSD([subQ0])],"isStart":true})})});}
            var Q10;
            {var subQ0=sQuery(id+"F6.wireOp",EDGE,"E20.left");Q10=makeQuery(id+"F11.boolean.opBoolean","SPLIT",EDGE,{"disambiguationData":[TD([makeQuery(id+"F7.boolean.opBoolean","COPY",FACE,{"derivedFrom":makeQuery(id+"F7.opExtrude","SWEPT_FACE",FACE,{"disambiguationData":[OSD([sQuery(id+"F6.wireOp",EDGE,"E20.bottom")])]})})])],"derivedFrom":makeQuery(id+"F7.boolean.opBoolean","COPY",EDGE,{"derivedFrom":makeQuery(id+"F7.opExtrude","CAP_EDGE",EDGE,{"disambiguationData":[OSD([subQ0])],"isStart":true})})});}
            var Q11;
            Q11=makeQuery(id+"F18.boolean.opBoolean","INTERSECT",EDGE,{"derivedFrom":[makeQuery(id+"F16.boolean.opBoolean","COPY",FACE,{"derivedFrom":makeQuery(id+"F16.opExtrude","SWEPT_FACE",FACE,{"disambiguationData":[OSD([sQuery(id+"F15.wireOp",EDGE,"E32.top")])]})}),makeQuery(id+"F18.opExtrude","CAP_FACE",FACE,{"disambiguationData":[OSD([sQuery(id+"F17.wireOp",EDGE,"E33.bottom"),sQuery(id+"F17.wireOp",EDGE,"E33.top"),sQuery(id+"F17.wireOp",EDGE,"E33.left"),sQuery(id+"F17.wireOp",EDGE,"E33.right")])],"isStart":false})]});
            var Q12;
            Q12=makeQuery(id+"F18.boolean.opBoolean","INTERSECT",EDGE,{"derivedFrom":[makeQuery(id+"F16.boolean.opBoolean","COPY",FACE,{"derivedFrom":makeQuery(id+"F16.opExtrude","SWEPT_FACE",FACE,{"disambiguationData":[OSD([sQuery(id+"F15.wireOp",EDGE,"E32.bottom")])]})}),makeQuery(id+"F18.opExtrude","CAP_FACE",FACE,{"disambiguationData":[OSD([sQuery(id+"F17.wireOp",EDGE,"E33.bottom"),sQuery(id+"F17.wireOp",EDGE,"E33.top"),sQuery(id+"F17.wireOp",EDGE,"E33.left"),sQuery(id+"F17.wireOp",EDGE,"E33.right")])],"isStart":false})]});
            var Q13;
            Q13=makeQuery(id+"F1.opExtrude","CAP_EDGE",EDGE,{"disambiguationData":[OSD([sQuery(id+"F0.wireOp",EDGE,"E2")])],"isStart":false});
            var Q14;
            {var subQ0=sQuery(id+"F0.wireOp",EDGE,"E2");var subQ1=sQuery(id+"F0.wireOp",EDGE,"E1");Q14=makeQuery(id+"F11.boolean.opBoolean","SPLIT",EDGE,{"disambiguationData":[TD([makeQuery(id+"F1.opExtrude","SWEPT_FACE",FACE,{"disambiguationData":[OSD([subQ1])]})])],"derivedFrom":makeQuery(id+"F1.opExtrude","CAP_EDGE",EDGE,{"disambiguationData":[OSD([subQ0])],"isStart":true})});}
            var Q15;
            {var subQ0=sQuery(id+"F0.wireOp",EDGE,"E3");var subQ1=sQuery(id+"F0.wireOp",EDGE,"E2");Q15=makeQuery(id+"F11.boolean.opBoolean","SPLIT",EDGE,{"disambiguationData":[TD([makeQuery(id+"F1.opExtrude","SWEPT_FACE",FACE,{"disambiguationData":[OSD([subQ0])]})])],"derivedFrom":makeQuery(id+"F1.opExtrude","CAP_EDGE",EDGE,{"disambiguationData":[OSD([subQ1])],"isStart":true})});}
            var Q16;
            Q16=makeQuery(id+"F11.boolean.opBoolean","INTERSECT",EDGE,{"derivedFrom":[makeQuery(id+"F1.opExtrude","SWEPT_FACE",FACE,{"disambiguationData":[OSD([sQuery(id+"F0.wireOp",EDGE,"E2")])]}),makeQuery(id+"F11.opExtrude","CAP_FACE",FACE,{"disambiguationData":[OSD([sQuery(id+"F10.wireOp",EDGE,"E27.bottom"),sQuery(id+"F10.wireOp",EDGE,"E27.top"),sQuery(id+"F10.wireOp",EDGE,"E27.left"),sQuery(id+"F10.wireOp",EDGE,"E27.right")])],"isStart":false})]});
            var Q17;
            Q17=makeQuery(id+"F41.boolean.opBoolean","MERGE",EDGE,{"derivedFrom":[makeQuery(id+"F39.opExtrude","CAP_EDGE",EDGE,{"disambiguationData":[OSD([sQuery(id+"F38.wireOp",EDGE,"E75")])],"isStart":false}),makeQuery(id+"F39.opExtrude","CAP_EDGE",EDGE,{"disambiguationData":[OSD([sQuery(id+"F38.wireOp",EDGE,"E82.trimOffspring")])],"isStart":false}),makeQuery(id+"F41.opExtrude","CAP_EDGE",EDGE,{"disambiguationData":[OSD([sQuery(id+"F40.wireOp",EDGE,"E83")])],"isStart":false})]});
            fillet(context, id + "F43", {"entities" : qUnion([Q0, Q1, Q2, Q3, Q4, Q5, Q6, Q7, Q8, Q9, Q10, Q11, Q12, Q13, Q14, Q15, Q16, Q17]), "radius" : 2 * mm, "tangentPropagation" : true, "allowEdgeOverflow" : false});
        }
        {
            var Q0;
            Q0=makeQuery(id+"F39.boolean.opBoolean","MERGE",FACE,{"derivedFrom":[makeQuery(id+"F37.boolean.opBoolean","MERGE",FACE,{"derivedFrom":[makeQuery(id+"F1.opExtrude","SWEPT_FACE",FACE,{"disambiguationData":[OSD([sQuery(id+"F0.wireOp",EDGE,"E3")])]}),makeQuery(id+"F37.opExtrude","SWEPT_FACE",FACE,{"disambiguationData":[OSD([sQuery(id+"F36.wireOp",EDGE,"E66")])]})]}),makeQuery(id+"F39.opExtrude","SWEPT_FACE",FACE,{"disambiguationData":[OSD([sQuery(id+"F38.wireOp",EDGE,"E78")])]})]});
            var sketch = newSketch(context, id + "F44", { "sketchPlane" : qUnion([Q0])});
            skLineSegment(sketch, "E84.bottom", {"start": v(50, -35.64) * mm, "end": v(46, -35.64) * mm});
            skLineSegment(sketch, "E84.top", {"start": v(50, -31.64) * mm, "end": v(46, -31.64) * mm});
            skLineSegment(sketch, "E84.left", {"start": v(50, -35.64) * mm, "end": v(50, -31.64) * mm});
            skLineSegment(sketch, "E84.right", {"start": v(46, -35.64) * mm, "end": v(46, -31.64) * mm});
            skLineSegment(sketch, "E85.MirrorCS", {"start": v(-50, -31.64) * mm, "end": v(-46, -31.64) * mm});
            skLineSegment(sketch, "E86.MirrorCS", {"start": v(-46, -35.64) * mm, "end": v(-46, -31.64) * mm});
            skLineSegment(sketch, "E87.MirrorCS", {"start": v(-50, -35.64) * mm, "end": v(-46, -35.64) * mm});
            skLineSegment(sketch, "E88.MirrorCS", {"start": v(-50, -35.64) * mm, "end": v(-50, -31.64) * mm});
            skSolve(sketch);
        }
        {
            var Q0;
            Q0=qSketchRegion(id+"F44",true);
            extrude(context, id + "F45", {"entities" : qUnion([Q0]), "operationType" : NewBodyOperationType.ADD, "depth" : 5 * mm});
        }
        {
            var Q0;
            Q0=makeQuery(id+"F45.opExtrude","CAP_EDGE",EDGE,{"disambiguationData":[OSD([sQuery(id+"F44.wireOp",EDGE,"E87.MirrorCS")])],"isStart":false});
            var Q1;
            Q1=makeQuery(id+"F45.opExtrude","CAP_EDGE",EDGE,{"disambiguationData":[OSD([sQuery(id+"F44.wireOp",EDGE,"E86.MirrorCS")])],"isStart":false});
            var Q2;
            Q2=makeQuery(id+"F45.opExtrude","CAP_EDGE",EDGE,{"disambiguationData":[OSD([sQuery(id+"F44.wireOp",EDGE,"E88.MirrorCS")])],"isStart":false});
            var Q3;
            Q3=makeQuery(id+"F45.opExtrude","CAP_EDGE",EDGE,{"disambiguationData":[OSD([sQuery(id+"F44.wireOp",EDGE,"E85.MirrorCS")])],"isStart":false});
            var Q4;
            Q4=makeQuery(id+"F45.opExtrude","CAP_EDGE",EDGE,{"disambiguationData":[OSD([sQuery(id+"F44.wireOp",EDGE,"E84.left")])],"isStart":false});
            var Q5;
            Q5=makeQuery(id+"F45.opExtrude","CAP_EDGE",EDGE,{"disambiguationData":[OSD([sQuery(id+"F44.wireOp",EDGE,"E84.bottom")])],"isStart":false});
            var Q6;
            Q6=makeQuery(id+"F45.opExtrude","CAP_EDGE",EDGE,{"disambiguationData":[OSD([sQuery(id+"F44.wireOp",EDGE,"E84.right")])],"isStart":false});
            var Q7;
            Q7=makeQuery(id+"F45.opExtrude","CAP_EDGE",EDGE,{"disambiguationData":[OSD([sQuery(id+"F44.wireOp",EDGE,"E84.top")])],"isStart":false});
            fillet(context, id + "F46", {"entities" : qUnion([Q0, Q1, Q2, Q3, Q4, Q5, Q6, Q7]), "radius" : 2 * mm, "tangentPropagation" : true, "allowEdgeOverflow" : false});
        }
        {
            var Q0;
            {var subQ4=sQuery(id+"F8.wireOp",EDGE,"E26.0.startCap");Q0=makeQuery(id+"F8.imprint","IMPRINT",FACE,{"disambiguationData":[TD([[makeQuery(id+"F8.imprint","IMPRINT",EDGE,{"derivedFrom":subQ4}),-1.0]])]});}
            var sketch = newSketch(context, id + "F47", { "sketchPlane" : qUnion([Q0])});
            skCircle(sketch, "E89", {"center": v(-13, 47.5) * mm, "radius": 0.75 * mm});
            skCircle(sketch, "E90", {"center": v(-13, 12.5) * mm, "radius": 0.75 * mm});
            skSolve(sketch);
        }
        {
            var Q0;
            Q0=qSketchRegion(id+"F47",true);
            extrude(context, id + "F48", {"entities" : qUnion([Q0]), "operationType" : NewBodyOperationType.REMOVE, "oppositeDirection" : true, "depth" : 10 * mm});
        }
        {
            var Q0;
            {var subQ0=sQuery(id+"F17.wireOp",EDGE,"E33.bottom");var subQ1=sQuery(id+"F17.wireOp",EDGE,"E33.left");var subQ2=sQuery(id+"F17.wireOp",EDGE,"E33.right");Q0=makeQuery(id+"F18.boolean.opBoolean","COPY",FACE,{"disambiguationData":[TD([makeQuery(id+"F16.boolean.opBoolean","COPY",FACE,{"derivedFrom":makeQuery(id+"F16.opExtrude","SWEPT_FACE",FACE,{"disambiguationData":[OSD([sQuery(id+"F15.wireOp",EDGE,"E32.top")])]})})])],"derivedFrom":makeQuery(id+"F18.opExtrude","CAP_FACE",FACE,{"disambiguationData":[OSD([subQ0,sQuery(id+"F17.wireOp",EDGE,"E33.top"),subQ1,subQ2])],"isStart":false})});}
            var sketch = newSketch(context, id + "F49", { "sketchPlane" : qUnion([Q0])});
            skCircle(sketch, "E91", {"center": v(0, -24.64) * mm, "radius": 0.75 * mm});
            skPoint(sketch, "E92", {"position": v(0, -38.64) * mm});
            skCircle(sketch, "E93", {"center": v(0, -52.64) * mm, "radius": 0.75 * mm});
            skPoint(sketch, "E94.orphan", {"position": v(6.5, -25.14) * mm});
            skPoint(sketch, "E95.end.orphan", {"position": v(6.5, -52.14) * mm});
            skPoint(sketch, "E96.end.orphan", {"position": v(-6.5, -52.14) * mm});
            skSolve(sketch);
        }
        {
            var Q0;
            Q0=qSketchRegion(id+"F49",true);
            extrude(context, id + "F50", {"entities" : qUnion([Q0]), "operationType" : NewBodyOperationType.REMOVE, "oppositeDirection" : true, "depth" : 10 * mm});
        }
    });
